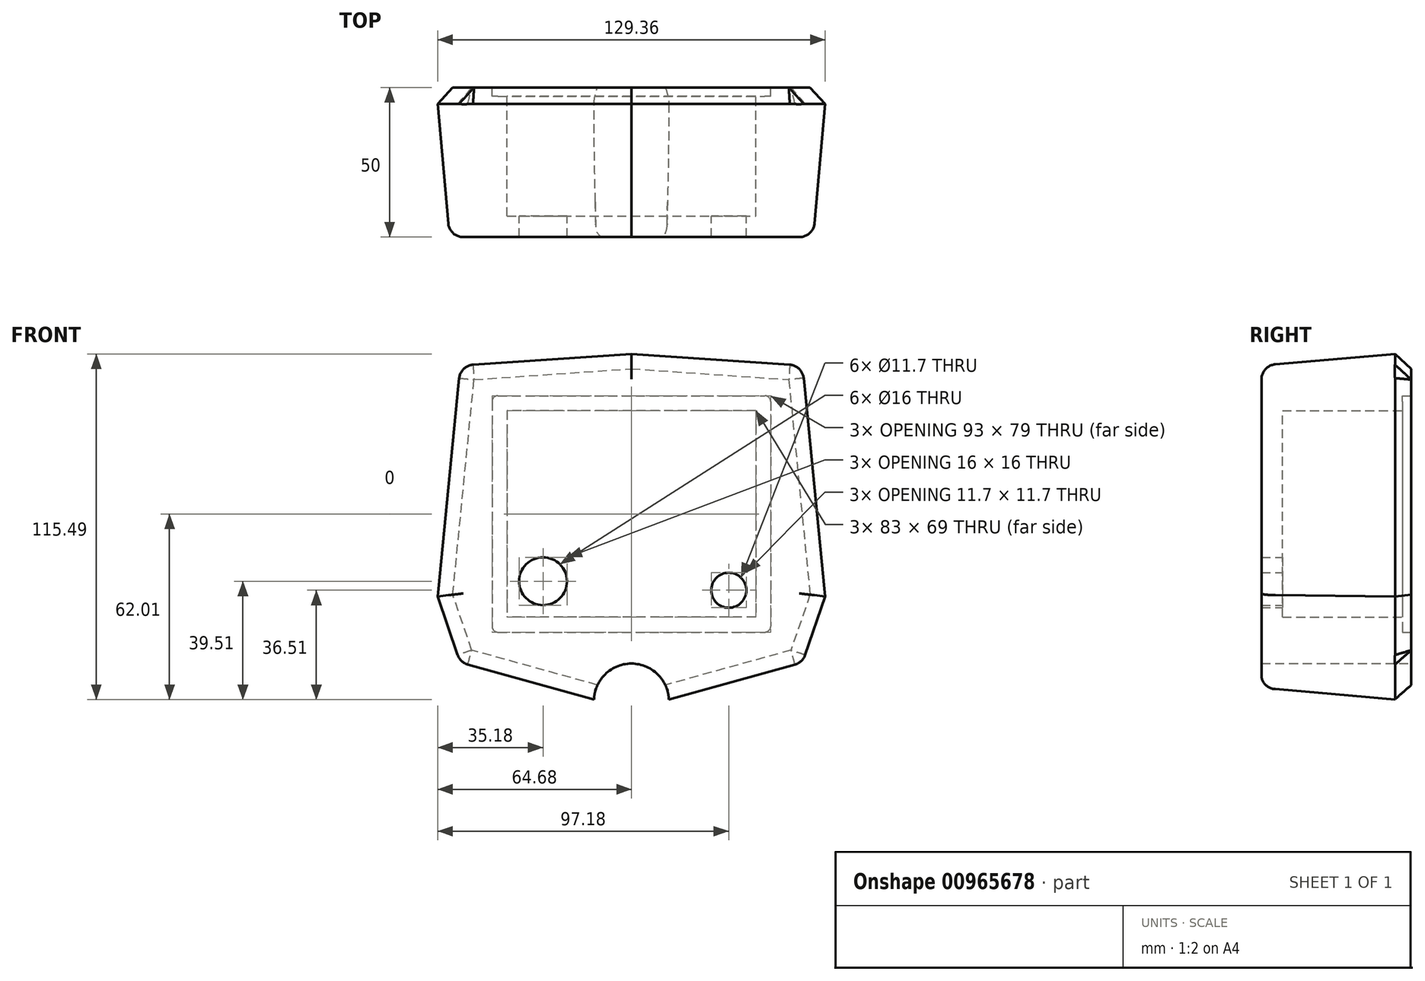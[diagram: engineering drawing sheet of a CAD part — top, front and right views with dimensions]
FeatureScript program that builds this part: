
annotation { "Feature Type Name" : "Feature", "Feature Type Description" : "" }
export const myFeature = defineFeature(function(context is Context, id is Id, definition is map)
    precondition{}
    {
        {
            var Q0;
            Q0=qCreatedBy(makeId("Front.planeOp"),FACE);
            var sketch = newSketch(context, id + "F0", { "sketchPlane" : qUnion([Q0])});
            skLineSegment(sketch, "E0.bottom", {"start": v(-44.5, 39.5) * mm, "end": v(44.5, 39.5) * mm});
            skLineSegment(sketch, "E0.top", {"start": v(-44.5, -39.5) * mm, "end": v(44.5, -39.5) * mm});
            skLineSegment(sketch, "E0.left", {"start": v(-46.5, 37.5) * mm, "end": v(-46.5, -37.5) * mm});
            skLineSegment(sketch, "E0.right", {"start": v(46.5, 37.5) * mm, "end": v(46.5, -37.5) * mm});
            skLineSegment(sketch, "E1.bottom", {"start": v(57.5, -50) * mm, "end": v(-57.5, -50) * mm});
            skLineSegment(sketch, "E1.top", {"start": v(57.5, 50) * mm, "end": v(-57.5, 50) * mm});
            skLineSegment(sketch, "E1.left", {"start": v(57.5, -50) * mm, "end": v(57.5, 50) * mm});
            skLineSegment(sketch, "E1.right", {"start": v(-57.5, -50) * mm, "end": v(-57.5, 50) * mm});
            skPoint(sketch, "E1.middle", {"position": v(0, 0) * mm});
            skPoint(sketch, "E1.middle.positionSnap0", {"position": v(-46.5, 0) * mm});
            skPoint(sketch, "E1.middle.positionSnap1", {"position": v(0, 39.5) * mm});
            skPoint(sketch, "E1.centerSnap0", {"position": v(-46.5, 0) * mm});
            skPoint(sketch, "E1.centerSnap1", {"position": v(0, 39.5) * mm});
            skLineSegment(sketch, "E2", {"start": v(0, 50) * mm, "end": v(0, -50) * mm, "construction": true});
            skLineSegment(sketch, "E3", {"start": v(-52.7, -2.38) * mm, "end": v(-52.7, -2.38) * mm});
            skArc(sketch, "E4", {"start": v(12.5, -62.5) * mm, "mid": v(0, -50) * mm, "end": v(-12.5, -62.5) * mm});
            skLineSegment(sketch, "E5", {"start": v(12.5, -62.5) * mm, "end": v(57.5, -50) * mm});
            skLineSegment(sketch, "E6", {"start": v(-12.5, -62.5) * mm, "end": v(-57.5, -50) * mm});
            skLineSegment(sketch, "E7", {"start": v(-57.5, 50) * mm, "end": v(0, 53.96) * mm});
            skLineSegment(sketch, "E8", {"start": v(0, 53.96) * mm, "end": v(57.5, 50) * mm});
            skLineSegment(sketch, "E9", {"start": v(57.5, 50) * mm, "end": v(65.16, -27.62) * mm});
            skLineSegment(sketch, "E10", {"start": v(65.16, -27.62) * mm, "end": v(57.5, -50) * mm});
            skLineSegment(sketch, "E11.MirrorCS", {"start": v(-57.5, 50) * mm, "end": v(-65.16, -27.62) * mm});
            skLineSegment(sketch, "E12.MirrorCS", {"start": v(-65.16, -27.62) * mm, "end": v(-57.5, -50) * mm});
            skLineSegment(sketch, "E13", {"start": v(-12.5, -62.5) * mm, "end": v(12.5, -62.5) * mm});
            skLineSegment(sketch, "E14.bottom", {"start": v(-41.5, -34.5) * mm, "end": v(41.5, -34.5) * mm});
            skLineSegment(sketch, "E14.top", {"start": v(-41.5, 34.5) * mm, "end": v(41.5, 34.5) * mm});
            skLineSegment(sketch, "E14.left", {"start": v(-41.5, -34.5) * mm, "end": v(-41.5, 34.5) * mm});
            skLineSegment(sketch, "E14.right", {"start": v(41.5, -34.5) * mm, "end": v(41.5, 34.5) * mm});
            skPoint(sketch, "E15.visualSharp", {"position": v(46.5, 39.5) * mm});
            skArc(sketch, "E15.filletArc", {"start": v(46.5, 37.5) * mm, "mid": v(45.91, 38.91) * mm, "end": v(44.5, 39.5) * mm});
            skPoint(sketch, "E16.visualSharp", {"position": v(-46.5, 39.5) * mm});
            skArc(sketch, "E16.filletArc", {"start": v(-44.5, 39.5) * mm, "mid": v(-45.91, 38.91) * mm, "end": v(-46.5, 37.5) * mm});
            skPoint(sketch, "E17.visualSharp", {"position": v(46.5, -39.5) * mm});
            skArc(sketch, "E17.filletArc", {"start": v(44.5, -39.5) * mm, "mid": v(45.91, -38.91) * mm, "end": v(46.5, -37.5) * mm});
            skPoint(sketch, "E18.visualSharp", {"position": v(-46.5, -39.5) * mm});
            skArc(sketch, "E18.filletArc", {"start": v(-46.5, -37.5) * mm, "mid": v(-45.91, -38.91) * mm, "end": v(-44.5, -39.5) * mm});
            skSolve(sketch);
        }
        {
            var Q0;
            Q0=makeQuery(id+"F0.imprint","IMPRINT",FACE,{"disambiguationData":[TD([[makeQuery(id+"F0.imprint","IMPRINT",EDGE,{"derivedFrom":sQuery(id+"F0.wireOp",EDGE,"E0.bottom")}),-1.0]])]});
            var Q1;
            Q1=makeQuery(id+"F0.imprint","IMPRINT",FACE,{"disambiguationData":[TD([[makeQuery(id+"F0.imprint","IMPRINT",EDGE,{"derivedFrom":sQuery(id+"F0.wireOp",EDGE,"E0.bottom")}),1.0]])]});
            var Q2;
            Q2=makeQuery(id+"F0.imprint","IMPRINT",FACE,{"disambiguationData":[TD([[makeQuery(id+"F0.imprint","IMPRINT",EDGE,{"derivedFrom":sQuery(id+"F0.wireOp",EDGE,"E1.right")}),1.0]])]});
            var Q3;
            {var subQ0=sQuery(id+"F0.wireOp",EDGE,"E6");Q3=makeQuery(id+"F0.imprint","IMPRINT",FACE,{"disambiguationData":[TD([[makeQuery(id+"F0.imprint","IMPRINT",EDGE,{"derivedFrom":subQ0}),-1.0]])]});}
            var Q4;
            {var subQ0=sQuery(id+"F0.wireOp",EDGE,"E13");Q4=makeQuery(id+"F0.imprint","IMPRINT",FACE,{"disambiguationData":[TD([[makeQuery(id+"F0.imprint","IMPRINT",EDGE,{"derivedFrom":subQ0}),1.0]])]});}
            var Q5;
            {var subQ0=sQuery(id+"F0.wireOp",EDGE,"E5");Q5=makeQuery(id+"F0.imprint","IMPRINT",FACE,{"disambiguationData":[TD([[makeQuery(id+"F0.imprint","IMPRINT",EDGE,{"derivedFrom":subQ0}),1.0]])]});}
            var Q6;
            Q6=makeQuery(id+"F0.imprint","IMPRINT",FACE,{"disambiguationData":[TD([[makeQuery(id+"F0.imprint","IMPRINT",EDGE,{"derivedFrom":sQuery(id+"F0.wireOp",EDGE,"E1.left")}),-1.0]])]});
            var Q7;
            Q7=makeQuery(id+"F0.imprint","IMPRINT",FACE,{"disambiguationData":[TD([[makeQuery(id+"F0.imprint","IMPRINT",EDGE,{"derivedFrom":sQuery(id+"F0.wireOp",EDGE,"E1.top")}),-1.0]])]});
            var Q8;
            Q8=makeQuery(id+"F0.imprint","IMPRINT",FACE,{"disambiguationData":[TD([[makeQuery(id+"F0.imprint","IMPRINT",EDGE,{"derivedFrom":sQuery(id+"F0.wireOp",EDGE,"E14.bottom")}),1.0]])]});
            extrude(context, id + "F1", {"entities" : qUnion([Q0, Q1, Q2, Q3, Q4, Q5, Q6, Q7, Q8]), "depth" : 50 * mm, "offsetDistance" : 25.4 * mm, "hasDraft" : true, "draftAngle" : 5 * degree, "draftPullDirection" : true});
        }
        {
            var Q0;
            {var subQ0=sQuery(id+"F0.wireOp",EDGE,"E13");Q0=makeQuery(id+"F0.imprint","IMPRINT",FACE,{"disambiguationData":[TD([[makeQuery(id+"F0.imprint","IMPRINT",EDGE,{"derivedFrom":subQ0}),1.0]])]});}
            extrude(context, id + "F2", {"entities" : qUnion([Q0]), "operationType" : NewBodyOperationType.REMOVE, "depth" : 50 * mm, "offsetDistance" : 25 * mm});
        }
        {
            var Q0;
            Q0=makeQuery(id+"F0.imprint","IMPRINT",FACE,{"disambiguationData":[TD([[makeQuery(id+"F0.imprint","IMPRINT",EDGE,{"derivedFrom":sQuery(id+"F0.wireOp",EDGE,"E0.bottom")}),-1.0]])]});
            var Q1;
            Q1=makeQuery(id+"F0.imprint","IMPRINT",FACE,{"disambiguationData":[TD([[makeQuery(id+"F0.imprint","IMPRINT",EDGE,{"derivedFrom":sQuery(id+"F0.wireOp",EDGE,"E14.bottom")}),1.0]])]});
            extrude(context, id + "F3", {"entities" : qUnion([Q0, Q1]), "operationType" : NewBodyOperationType.REMOVE, "depth" : 3 * mm, "offsetDistance" : 25 * mm});
        }
        {
            var Q0;
            Q0=makeQuery(id+"F0.imprint","IMPRINT",FACE,{"disambiguationData":[TD([[makeQuery(id+"F0.imprint","IMPRINT",EDGE,{"derivedFrom":sQuery(id+"F0.wireOp",EDGE,"E14.bottom")}),1.0]])]});
            extrude(context, id + "F4", {"entities" : qUnion([Q0]), "operationType" : NewBodyOperationType.REMOVE, "depth" : 43 * mm, "offsetDistance" : 25 * mm});
        }
        {
            var Q0;
            Q0=makeQuery(id+"F1.opExtrude","CAP_EDGE",EDGE,{"disambiguationData":[OSD([sQuery(id+"F0.wireOp",EDGE,"E7")])],"isStart":false});
            var Q1;
            Q1=makeQuery(id+"F1.opExtrude","CAP_EDGE",EDGE,{"disambiguationData":[OSD([sQuery(id+"F0.wireOp",EDGE,"E8")])],"isStart":false});
            var Q2;
            Q2=makeQuery(id+"F1.opExtrude","CAP_EDGE",EDGE,{"disambiguationData":[OSD([sQuery(id+"F0.wireOp",EDGE,"E9")])],"isStart":false});
            var Q3;
            Q3=makeQuery(id+"F1.opExtrude","CAP_EDGE",EDGE,{"disambiguationData":[OSD([sQuery(id+"F0.wireOp",EDGE,"E10")])],"isStart":false});
            var Q4;
            Q4=makeQuery(id+"F1.opExtrude","CAP_EDGE",EDGE,{"disambiguationData":[OSD([sQuery(id+"F0.wireOp",EDGE,"E11.MirrorCS")])],"isStart":false});
            var Q5;
            Q5=makeQuery(id+"F1.opExtrude","CAP_EDGE",EDGE,{"disambiguationData":[OSD([sQuery(id+"F0.wireOp",EDGE,"E12.MirrorCS")])],"isStart":false});
            var Q6;
            Q6=makeQuery(id+"F1.opExtrude","CAP_EDGE",EDGE,{"disambiguationData":[OSD([sQuery(id+"F0.wireOp",EDGE,"E5")])],"isStart":false});
            var Q7;
            Q7=makeQuery(id+"F1.opExtrude","CAP_EDGE",EDGE,{"disambiguationData":[OSD([sQuery(id+"F0.wireOp",EDGE,"E6")])],"isStart":false});
            var Q8;
            Q8=makeQuery(id+"F2.boolean.opBoolean","COPY",EDGE,{"derivedFrom":makeQuery(id+"F2.opExtrude","CAP_EDGE",EDGE,{"disambiguationData":[OSD([sQuery(id+"F0.wireOp",EDGE,"E4")])],"isStart":false})});
            var Q9;
            Q9=makeQuery(id+"F1.opExtrude","SWEPT_EDGE",EDGE,{"disambiguationData":[OSD([sQuery(id+"F0.wireOp",EDGE,"E1.top"),sQuery(id+"F0.wireOp",EDGE,"E1.right"),sQuery(id+"F0.wireOp",EDGE,"E7"),sQuery(id+"F0.wireOp",EDGE,"E11.MirrorCS")])]});
            var Q10;
            Q10=makeQuery(id+"F1.opExtrude","SWEPT_EDGE",EDGE,{"disambiguationData":[OSD([sQuery(id+"F0.wireOp",EDGE,"E1.top"),sQuery(id+"F0.wireOp",EDGE,"E1.left"),sQuery(id+"F0.wireOp",EDGE,"E8"),sQuery(id+"F0.wireOp",EDGE,"E9")])]});
            var Q11;
            Q11=makeQuery(id+"F1.opExtrude","SWEPT_EDGE",EDGE,{"disambiguationData":[OSD([sQuery(id+"F0.wireOp",EDGE,"E1.bottom"),sQuery(id+"F0.wireOp",EDGE,"E1.left"),sQuery(id+"F0.wireOp",EDGE,"E5"),sQuery(id+"F0.wireOp",EDGE,"E10")])]});
            var Q12;
            Q12=makeQuery(id+"F1.opExtrude","SWEPT_EDGE",EDGE,{"disambiguationData":[OSD([sQuery(id+"F0.wireOp",EDGE,"E1.bottom"),sQuery(id+"F0.wireOp",EDGE,"E1.right"),sQuery(id+"F0.wireOp",EDGE,"E6"),sQuery(id+"F0.wireOp",EDGE,"E12.MirrorCS")])]});
            fillet(context, id + "F5", {"entities" : qUnion([Q0, Q1, Q2, Q3, Q4, Q5, Q6, Q7, Q8, Q9, Q10, Q11, Q12]), "radius" : 5 * mm, "tangentPropagation" : true, "allowEdgeOverflow" : false});
        }
        {
            var Q0;
            Q0=makeQuery(id+"F1.opExtrude","CAP_EDGE",EDGE,{"disambiguationData":[OSD([sQuery(id+"F0.wireOp",EDGE,"E8")])],"isStart":true});
            var Q1;
            Q1=makeQuery(id+"F1.opExtrude","CAP_EDGE",EDGE,{"disambiguationData":[OSD([sQuery(id+"F0.wireOp",EDGE,"E7")])],"isStart":true});
            var Q2;
            Q2=makeQuery(id+"F1.opExtrude","CAP_EDGE",EDGE,{"disambiguationData":[OSD([sQuery(id+"F0.wireOp",EDGE,"E10")])],"isStart":true});
            var Q3;
            Q3=makeQuery(id+"F1.opExtrude","CAP_EDGE",EDGE,{"disambiguationData":[OSD([sQuery(id+"F0.wireOp",EDGE,"E12.MirrorCS")])],"isStart":true});
            chamfer(context, id + "F6", {"entities" : qUnion([Q0, Q1, Q2, Q3]), "width" : 5 * mm, "tangentPropagation" : true});
        }
        {
            var Q0;
            Q0=makeQuery(id+"F4.boolean.opBoolean","COPY",FACE,{"derivedFrom":makeQuery(id+"F4.opExtrude","CAP_FACE",FACE,{"disambiguationData":[OSD([sQuery(id+"F0.wireOp",EDGE,"E14.bottom"),sQuery(id+"F0.wireOp",EDGE,"E14.top"),sQuery(id+"F0.wireOp",EDGE,"E14.left"),sQuery(id+"F0.wireOp",EDGE,"E14.right")])],"isStart":false})});
            var sketch = newSketch(context, id + "F7", { "sketchPlane" : qUnion([Q0])});
            skCircle(sketch, "E19", {"center": v(29.5, -22.5) * mm, "radius": 11 * mm});
            skCircle(sketch, "E20", {"center": v(29.5, -22.5) * mm, "radius": 8 * mm});
            skCircle(sketch, "E21", {"center": v(-32.5, -25.5) * mm, "radius": 8 * mm});
            skCircle(sketch, "E22", {"center": v(-32.5, -25.5) * mm, "radius": 5.85 * mm});
            skSolve(sketch);
        }
        {
            var Q0;
            Q0=makeQuery(id+"F7.imprint","IMPRINT",FACE,{"disambiguationData":[TD([[makeQuery(id+"F7.imprint","IMPRINT",EDGE,{"derivedFrom":sQuery(id+"F7.wireOp",EDGE,"E22")}),1.0]])]});
            extrude(context, id + "F8", {"entities" : qUnion([Q0]), "operationType" : NewBodyOperationType.REMOVE, "endBound" : BoundingType.UP_TO_NEXT, "oppositeDirection" : true, "depth" : 25 * mm, "offsetDistance" : 25 * mm});
        }
        {
            var Q0;
            Q0=makeQuery(id+"F7.imprint","IMPRINT",FACE,{"disambiguationData":[TD([[makeQuery(id+"F7.imprint","IMPRINT",EDGE,{"derivedFrom":sQuery(id+"F7.wireOp",EDGE,"E20")}),1.0]])]});
            extrude(context, id + "F9", {"entities" : qUnion([Q0]), "operationType" : NewBodyOperationType.REMOVE, "endBound" : BoundingType.UP_TO_NEXT, "oppositeDirection" : true, "depth" : 25 * mm, "offsetDistance" : 25 * mm});
        }
    });
